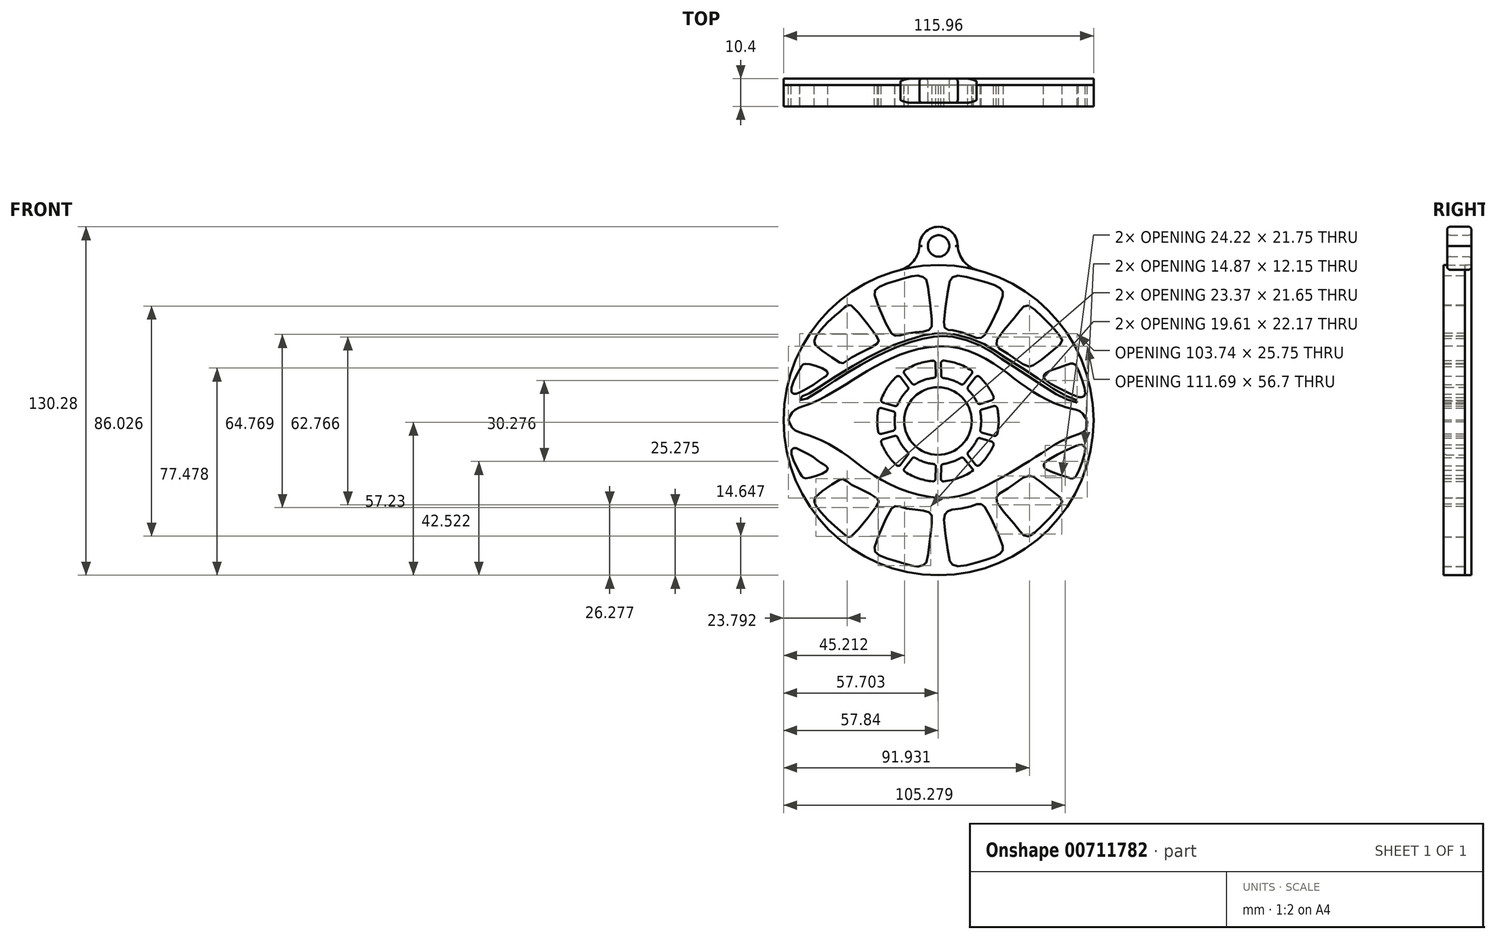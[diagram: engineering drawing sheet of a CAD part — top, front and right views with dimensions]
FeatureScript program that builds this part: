
annotation { "Feature Type Name" : "Feature", "Feature Type Description" : "" }
export const myFeature = defineFeature(function(context is Context, id is Id, definition is map)
    precondition{}
    {
        {
            var Q0;
            Q0=qCreatedBy(makeId("Front.planeOp"),FACE);
            var sketch = newSketch(context, id + "F0", { "sketchPlane" : qUnion([Q0])});
            skPoint(sketch, "E0.first.point", {"position": v(-56.19, 0) * mm});
            skPoint(sketch, "E0.second.point", {"position": v(55.8, -3.23) * mm});
            skPoint(sketch, "E0.third.point", {"position": v(-2.74, 55.09) * mm});
            skCircle(sketch, "E1", {"center": v(-0.25, -2.32) * mm, "radius": 12.63 * mm});
            skPoint(sketch, "E1.first.point", {"position": v(-12.67, 0) * mm});
            skPoint(sketch, "E1.second.point", {"position": v(12.27, -3.96) * mm});
            skPoint(sketch, "E1.third.point", {"position": v(2.35, 10.04) * mm});
            skFitSpline(sketch, "E2", {"points": [v(0, 25.6) * mm, v(22.08, 18.16) * mm, v(35.62, 8.4) * mm, v(48.16, 2.67) * mm, v(53.12, 1.17) * mm, v(55.8, -3.23) * mm], "startDerivative": vector(97.64, 3.3) * mm, "endDerivative": vector(12.94, -38.95) * mm});
            skFitSpline(sketch, "E3.MirrorCS", {"points": [v(0, 25.6) * mm, v(-22.75, 18.54) * mm, v(-38.1, 9.34) * mm, v(-48.7, 3.85) * mm, v(-54.13, 1.57) * mm, v(-56.3, -2.43) * mm], "startDerivative": vector(-92.15, -2.88) * mm, "endDerivative": vector(-12.94, -38.95) * mm});
            skFitSpline(sketch, "E4.MirrorCS", {"points": [v(0, -31.1) * mm, v(23.23, -23.62) * mm, v(36.64, -15.57) * mm, v(48.14, -8.8) * mm, v(55.17, -5.48) * mm, v(55.8, -1.41) * mm], "startDerivative": vector(97.64, -3.3) * mm, "endDerivative": vector(12.94, 38.95) * mm});
            skFitSpline(sketch, "E5.MirrorCS", {"points": [v(0, -31.1) * mm, v(-23.18, -23.24) * mm, v(-36.31, -13.78) * mm, v(-48.45, -7.65) * mm, v(-54.13, -5.41) * mm, v(-56.3, -1.41) * mm], "startDerivative": vector(-89.64, 6.19) * mm, "endDerivative": vector(-12.94, 38.95) * mm});
            skFitSpline(sketch, "E6", {"points": [v(-52, 5.4) * mm, v(-45.96, 7.88) * mm, v(-34.5, 15.43) * mm, v(-23.54, 21.65) * mm, v(-15.7, 25.25) * mm, v(-4.7, 28.68) * mm, v(0.44, 29.22) * mm], "startDerivative": vector(38.04, 9.99) * mm, "endDerivative": vector(34.79, 0.33) * mm});
            skFitSpline(sketch, "E7.MirrorCS", {"points": [v(51.82, 4.54) * mm, v(45.93, 6.75) * mm, v(33.9, 14.77) * mm, v(22.85, 21.49) * mm, v(15.76, 25.71) * mm, v(4.84, 29.15) * mm, v(-0.2, 29.2) * mm], "startDerivative": vector(-38.04, 9.99) * mm, "endDerivative": vector(-34.83, 0.37) * mm});
            skFitSpline(sketch, "E8", {"points": [v(-52.01, 8.4) * mm, v(-46.87, 11.2) * mm, v(-43.44, 13.7) * mm, v(-41.72, 14.8) * mm, v(-41.72, 16.2) * mm, v(-48.74, 19) * mm, v(-50.6, 18.84) * mm, v(-51.7, 17.29) * mm, v(-55.1, 9.31) * mm, v(-54.04, 7.78) * mm, v(-52.01, 8.4) * mm]});
            skFitSpline(sketch, "E9", {"points": [v(-45.87, 29.35) * mm, v(-40.77, 35.19) * mm, v(-36.51, 38.99) * mm, v(-34.47, 40.65) * mm, v(-33.45, 41.12) * mm, v(-32.25, 40.56) * mm, v(-22.8, 28.88) * mm, v(-22.42, 27.59) * mm, v(-23.26, 26.38) * mm, v(-31.7, 21.93) * mm, v(-34.29, 20.17) * mm, v(-35.96, 19.25) * mm, v(-37.62, 19.99) * mm, v(-45.96, 25.92) * mm, v(-46.52, 27.4) * mm, v(-45.87, 29.35) * mm]});
            skFitSpline(sketch, "E10", {"points": [v(-22.16, 47.89) * mm, v(-16.65, 49.92) * mm, v(-11.8, 51.3) * mm, v(-8.4, 52.08) * mm, v(-6.5, 51.82) * mm, v(-4.85, 50.9) * mm, v(-4.26, 49.4) * mm, v(-2.5, 34.19) * mm, v(-2.82, 32.55) * mm, v(-3.94, 31.57) * mm, v(-7.28, 30.98) * mm, v(-12.46, 30.26) * mm, v(-15.08, 29.54) * mm, v(-16.52, 29.6) * mm, v(-17.83, 30.72) * mm, v(-23.93, 44.67) * mm, v(-23.8, 46.44) * mm, v(-22.16, 47.89) * mm]});
            skFitSpline(sketch, "E11", {"points": [v(7.16, 52.01) * mm, v(14.24, 50.57) * mm, v(20.86, 48.54) * mm, v(23.28, 47.1) * mm, v(24, 46.05) * mm, v(24.07, 44.54) * mm, v(17.38, 30) * mm, v(16.07, 28.88) * mm, v(14.76, 28.62) * mm, v(11.75, 29.73) * mm, v(5.3, 31.6) * mm, v(3.6, 31.77) * mm, v(2.44, 32.42) * mm, v(2.05, 34.19) * mm, v(4.01, 49.2) * mm, v(5, 51.3) * mm, v(7.16, 52.01) * mm]});
            skFitSpline(sketch, "E12", {"points": [v(21.84, 28.1) * mm, v(29.38, 37.4) * mm, v(31.34, 40.02) * mm, v(32.78, 40.87) * mm, v(34.42, 40.48) * mm, v(39.47, 35.96) * mm, v(42.94, 32.35) * mm, v(45.37, 29.4) * mm, v(46.22, 27.83) * mm, v(45.56, 26.32) * mm, v(43.27, 24.55) * mm, v(39.53, 21.47) * mm, v(34.88, 18.2) * mm, v(33.96, 18.06) * mm, v(31.34, 19.05) * mm, v(26.69, 22.4) * mm, v(21.97, 25.4) * mm, v(21.64, 26.32) * mm, v(21.84, 28.1) * mm]});
            skFitSpline(sketch, "E13", {"points": [v(39.86, 15.5) * mm, v(48.7, 18.92) * mm, v(49.82, 19.24) * mm, v(50.87, 18.85) * mm, v(51.6, 18.13) * mm, v(54.84, 8.73) * mm, v(54.41, 6.99) * mm, v(53.17, 6.53) * mm, v(51.4, 6.99) * mm, v(44.78, 10.07) * mm, v(39.47, 13.54) * mm, v(39.27, 14.33) * mm, v(39.86, 15.5) * mm]});
            skFitSpline(sketch, "E14.MirrorC", {"points": [v(39.86, -20.15) * mm, v(48.7, -23.56) * mm, v(49.82, -23.88) * mm, v(50.87, -23.5) * mm, v(51.6, -22.77) * mm, v(54.84, -13.37) * mm, v(54.41, -11.63) * mm, v(53.17, -11.17) * mm, v(51.4, -11.63) * mm, v(44.78, -14.7) * mm, v(39.47, -18.18) * mm, v(39.27, -18.97) * mm, v(39.86, -20.15) * mm]});
            skFitSpline(sketch, "E15.MirrorC", {"points": [v(21.84, -32.73) * mm, v(29.38, -42.04) * mm, v(31.34, -44.66) * mm, v(32.78, -45.51) * mm, v(34.42, -45.12) * mm, v(39.47, -40.6) * mm, v(42.94, -37) * mm, v(45.37, -34.04) * mm, v(46.22, -32.47) * mm, v(45.56, -30.96) * mm, v(43.27, -29.2) * mm, v(39.53, -26.11) * mm, v(34.88, -22.84) * mm, v(33.96, -22.7) * mm, v(31.34, -23.69) * mm, v(26.69, -27.03) * mm, v(21.97, -30.04) * mm, v(21.64, -30.96) * mm, v(21.84, -32.73) * mm]});
            skFitSpline(sketch, "E16.MirrorC", {"points": [v(7.16, -56.65) * mm, v(14.24, -55.21) * mm, v(20.86, -53.18) * mm, v(23.28, -51.74) * mm, v(24, -50.69) * mm, v(24.07, -49.18) * mm, v(17.38, -34.63) * mm, v(16.07, -33.52) * mm, v(14.76, -33.26) * mm, v(11.75, -34.37) * mm, v(5.06, -35.48) * mm, v(3.5, -36) * mm, v(2.44, -37.06) * mm, v(2.05, -38.83) * mm, v(4.01, -53.83) * mm, v(5, -55.93) * mm, v(7.16, -56.65) * mm]});
            skFitSpline(sketch, "E17.MirrorC", {"points": [v(-22.16, -52.53) * mm, v(-16.65, -54.56) * mm, v(-11.8, -55.93) * mm, v(-8.4, -56.72) * mm, v(-6.5, -56.46) * mm, v(-4.85, -55.54) * mm, v(-4.26, -54.03) * mm, v(-2.5, -38.83) * mm, v(-2.82, -37.19) * mm, v(-3.94, -36.2) * mm, v(-7.28, -35.62) * mm, v(-12.46, -34.9) * mm, v(-15.08, -34.18) * mm, v(-16.52, -34.24) * mm, v(-17.83, -35.35) * mm, v(-23.93, -49.31) * mm, v(-23.8, -51.08) * mm, v(-22.16, -52.53) * mm]});
            skFitSpline(sketch, "E18.MirrorC", {"points": [v(-45.87, -33.99) * mm, v(-40.77, -39.83) * mm, v(-36.51, -43.63) * mm, v(-34.47, -45.3) * mm, v(-33.45, -45.76) * mm, v(-32.25, -45.2) * mm, v(-22.8, -33.52) * mm, v(-22.42, -32.23) * mm, v(-23.26, -31.02) * mm, v(-31.7, -26.57) * mm, v(-34.29, -24.81) * mm, v(-35.96, -23.89) * mm, v(-37.62, -24.63) * mm, v(-45.96, -30.56) * mm, v(-46.52, -32.04) * mm, v(-45.87, -33.99) * mm]});
            skFitSpline(sketch, "E19.MirrorC", {"points": [v(-52.01, -13.04) * mm, v(-46.87, -15.85) * mm, v(-43.44, -18.34) * mm, v(-41.72, -19.43) * mm, v(-41.72, -20.83) * mm, v(-48.74, -23.64) * mm, v(-50.6, -23.48) * mm, v(-51.7, -21.93) * mm, v(-55.1, -13.95) * mm, v(-54.04, -12.42) * mm, v(-52.01, -13.04) * mm]});
            skCircle(sketch, "E20", {"center": v(-0.25, -2.32) * mm, "radius": 58.34 * mm});
            skLineSegment(sketch, "E21.0", {"start": v(-9.43, 11) * mm, "end": v(-13.4, 16.13) * mm});
            skLineSegment(sketch, "E22.0", {"start": v(-10.98, 9.8) * mm, "end": v(-14.95, 14.97) * mm});
            skLineSegment(sketch, "E23.0", {"start": v(0.96, 13.83) * mm, "end": v(0.85, 20.35) * mm});
            skLineSegment(sketch, "E24.0", {"start": v(-0.95, 13.84) * mm, "end": v(-1.17, 20.31) * mm});
            skLineSegment(sketch, "E25.0", {"start": v(-15.55, 3.05) * mm, "end": v(-21.8, 4.82) * mm});
            skLineSegment(sketch, "E26.0", {"start": v(-16.08, 1.06) * mm, "end": v(-22.35, 2.79) * mm});
            skLineSegment(sketch, "E27.0", {"start": v(10.52, 9.8) * mm, "end": v(14.52, 14.93) * mm});
            skLineSegment(sketch, "E28.0", {"start": v(8.94, 11.01) * mm, "end": v(13.03, 16.08) * mm});
            skLineSegment(sketch, "E29.0", {"start": v(15.4, 1.82) * mm, "end": v(21.68, 3.5) * mm});
            skLineSegment(sketch, "E30.0", {"start": v(14.75, 3.82) * mm, "end": v(20.93, 5.8) * mm});
            skPoint(sketch, "E31.MirrorP", {"position": v(2.35, -14.68) * mm});
            skLineSegment(sketch, "E32.MirrorCS", {"start": v(10.52, -14.43) * mm, "end": v(14.52, -19.57) * mm});
            skLineSegment(sketch, "E33.MirrorCS", {"start": v(8.94, -15.65) * mm, "end": v(13.03, -20.72) * mm});
            skLineSegment(sketch, "E34.MirrorCS", {"start": v(-10.98, -14.44) * mm, "end": v(-14.95, -19.61) * mm});
            skLineSegment(sketch, "E35.MirrorCS", {"start": v(-9.43, -15.64) * mm, "end": v(-13.4, -20.77) * mm});
            skLineSegment(sketch, "E36.MirrorCS", {"start": v(-15.55, -7.7) * mm, "end": v(-21.8, -9.46) * mm});
            skLineSegment(sketch, "E37.MirrorCS", {"start": v(0.96, -18.47) * mm, "end": v(0.85, -24.99) * mm});
            skLineSegment(sketch, "E38.MirrorCS", {"start": v(-0.95, -18.48) * mm, "end": v(-1.17, -24.95) * mm});
            skLineSegment(sketch, "E39.MirrorCS", {"start": v(-16.08, -5.7) * mm, "end": v(-22.35, -7.43) * mm});
            skLineSegment(sketch, "E40.MirrorCS", {"start": v(15.4, -6.46) * mm, "end": v(21.68, -8.14) * mm});
            skLineSegment(sketch, "E41.MirrorCS", {"start": v(14.75, -8.46) * mm, "end": v(20.93, -10.43) * mm});
            skFitSpline(sketch, "E42.0", {"points": [v(-52.25, 6.37) * mm, v(-51.49, 6.57) * mm, v(-50.3, 6.95) * mm, v(-48.53, 7.68) * mm, v(-47.12, 8.37) * mm, v(-45.6, 9.23) * mm, v(-43.96, 10.25) * mm, v(-42.24, 11.4) * mm, v(-40.44, 12.62) * mm, v(-38.6, 13.9) * mm, v(-36.7, 15.18) * mm, v(-34.8, 16.44) * mm, v(-32.9, 17.62) * mm, v(-31.02, 18.74) * mm, v(-29.17, 19.78) * mm, v(-27.39, 20.76) * mm, v(-25.68, 21.67) * mm, v(-24.05, 22.52) * mm, v(-22.52, 23.3) * mm, v(-21.04, 24.02) * mm, v(-19.56, 24.72) * mm, v(-18.01, 25.4) * mm, v(-16.36, 26.07) * mm, v(-14.53, 26.77) * mm, v(-11.95, 27.7) * mm, v(-9.26, 28.56) * mm, v(-6.72, 29.25) * mm, v(-4.95, 29.67) * mm, v(-3.37, 29.95) * mm, v(-1.5, 30.17) * mm, v(-0.3, 30.2) * mm, v(0.44, 30.22) * mm]});
            skFitSpline(sketch, "E43.0", {"points": [v(52.07, 5.5) * mm, v(51.29, 5.71) * mm, v(50.09, 6.04) * mm, v(48.35, 6.7) * mm, v(47.19, 7.22) * mm, v(46.2, 7.74) * mm, v(45.16, 8.33) * mm, v(43.78, 9.19) * mm, v(42.02, 10.37) * mm, v(40.17, 11.65) * mm, v(38.28, 12.98) * mm, v(36.34, 14.34) * mm, v(34.39, 15.66) * mm, v(32.44, 16.9) * mm, v(30.53, 18.08) * mm, v(28.68, 19.18) * mm, v(26.9, 20.22) * mm, v(25.23, 21.2) * mm, v(23.68, 22.14) * mm, v(22.27, 23.04) * mm, v(20.92, 23.91) * mm, v(19.57, 24.77) * mm, v(18.15, 25.61) * mm, v(16.58, 26.44) * mm, v(14.81, 27.26) * mm, v(12.88, 28.03) * mm, v(10.88, 28.74) * mm, v(8.87, 29.34) * mm, v(7.24, 29.75) * mm, v(6, 30) * mm, v(5.12, 30.13) * mm, v(4.28, 30.22) * mm, v(3.23, 30.29) * mm, v(2.06, 30.28) * mm, v(0.84, 30.23) * mm, v(0.14, 30.2) * mm, v(-0.2, 30.2) * mm]});
            skLineSegment(sketch, "E44", {"start": v(-0.2, 29.2) * mm, "end": v(0.44, 29.22) * mm});
            skLineSegment(sketch, "E45", {"start": v(-52.25, 6.37) * mm, "end": v(-52, 5.4) * mm});
            skLineSegment(sketch, "E46", {"start": v(51.96, 5.53) * mm, "end": v(51.82, 4.54) * mm});
            skArc(sketch, "E47", {"start": v(-9.43, 11) * mm, "mid": v(-5.39, 13.01) * mm, "end": v(-0.95, 13.84) * mm});
            skArc(sketch, "E48", {"start": v(0.96, 13.83) * mm, "mid": v(5.14, 12.95) * mm, "end": v(8.94, 11.01) * mm});
            skArc(sketch, "E49", {"start": v(10.52, 9.8) * mm, "mid": v(12.98, 7.05) * mm, "end": v(14.75, 3.82) * mm});
            skArc(sketch, "E50", {"start": v(-15.55, 3.05) * mm, "mid": v(-13.71, 6.73) * mm, "end": v(-11, 9.82) * mm});
            skArc(sketch, "E51", {"start": v(-16.08, -5.7) * mm, "mid": v(-16.43, -2.32) * mm, "end": v(-16.08, 1.06) * mm});
            skArc(sketch, "E52", {"start": v(-15.55, -7.7) * mm, "mid": v(-13.71, -11.37) * mm, "end": v(-11, -14.46) * mm});
            skArc(sketch, "E53", {"start": v(-9.43, -15.64) * mm, "mid": v(-5.39, -17.65) * mm, "end": v(-0.95, -18.48) * mm});
            skArc(sketch, "E54", {"start": v(0.96, -18.47) * mm, "mid": v(5.14, -17.6) * mm, "end": v(8.94, -15.65) * mm});
            skArc(sketch, "E55", {"start": v(10.52, -14.43) * mm, "mid": v(12.98, -11.69) * mm, "end": v(14.75, -8.46) * mm});
            skArc(sketch, "E56", {"start": v(15.4, -6.46) * mm, "mid": v(15.93, -2.32) * mm, "end": v(15.4, 1.82) * mm});
            skArc(sketch, "E57", {"start": v(-13.4, 16.13) * mm, "mid": v(-7.59, 19.11) * mm, "end": v(-1.17, 20.31) * mm});
            skArc(sketch, "E58", {"start": v(0.85, 20.35) * mm, "mid": v(7.25, 19.1) * mm, "end": v(13.03, 16.08) * mm});
            skArc(sketch, "E59", {"start": v(-21.8, 4.82) * mm, "mid": v(-19.07, 10.37) * mm, "end": v(-14.95, 14.97) * mm});
            skArc(sketch, "E60", {"start": v(-22.35, -7.43) * mm, "mid": v(-22.93, -2.32) * mm, "end": v(-22.35, 2.79) * mm});
            skArc(sketch, "E61", {"start": v(-21.8, -9.46) * mm, "mid": v(-19.05, -15) * mm, "end": v(-14.92, -19.58) * mm});
            skArc(sketch, "E62", {"start": v(14.52, 14.93) * mm, "mid": v(18.3, 10.76) * mm, "end": v(20.92, 5.79) * mm});
            skArc(sketch, "E63", {"start": v(21.68, 3.5) * mm, "mid": v(22.44, -2.32) * mm, "end": v(21.68, -8.14) * mm});
            skArc(sketch, "E64", {"start": v(20.93, -10.43) * mm, "mid": v(18.27, -15.37) * mm, "end": v(14.47, -19.5) * mm});
            skArc(sketch, "E65", {"start": v(13.03, -20.72) * mm, "mid": v(7.25, -23.74) * mm, "end": v(0.85, -24.99) * mm});
            skArc(sketch, "E66", {"start": v(-1.17, -24.95) * mm, "mid": v(-7.59, -23.75) * mm, "end": v(-13.4, -20.77) * mm});
            skSolve(sketch);
        }
        {
            var Q0;
            Q0=qCreatedBy(makeId("Front.planeOp"),FACE);
            var sketch = newSketch(context, id + "F1", { "sketchPlane" : qUnion([Q0])});
            skCircle(sketch, "E67", {"center": v(0, -2) * mm, "radius": 57.98 * mm});
            skSolve(sketch);
        }
        {
            var Q0;
            Q0=qSketchRegion(id+"F1",true);
            extrude(context, id + "F2", {"entities" : qUnion([Q0]), "depth" : 8 * mm, "offsetDistance" : 25 * mm});
        }
        {
            var Q0;
            Q0=qSketchRegion(id+"F1",true);
            extrude(context, id + "F3", {"entities" : qUnion([Q0]), "oppositeDirection" : true, "depth" : 2.4 * mm, "offsetDistance" : 25 * mm});
        }
        {
            var Q0;
            Q0=makeQuery(id+"F0.imprint","IMPRINT",FACE,{"disambiguationData":[TD([[makeQuery(id+"F0.imprint","IMPRINT",EDGE,{"derivedFrom":sQuery(id+"F0.wireOp",EDGE,"E9")}),-1.0]])]});
            var Q1;
            Q1=makeQuery(id+"F0.imprint","IMPRINT",FACE,{"disambiguationData":[TD([[makeQuery(id+"F0.imprint","IMPRINT",EDGE,{"derivedFrom":sQuery(id+"F0.wireOp",EDGE,"E10")}),-1.0]])]});
            var Q2;
            Q2=makeQuery(id+"F0.imprint","IMPRINT",FACE,{"disambiguationData":[TD([[makeQuery(id+"F0.imprint","IMPRINT",EDGE,{"derivedFrom":sQuery(id+"F0.wireOp",EDGE,"E11")}),-1.0]])]});
            var Q3;
            Q3=makeQuery(id+"F0.imprint","IMPRINT",FACE,{"disambiguationData":[TD([[makeQuery(id+"F0.imprint","IMPRINT",EDGE,{"derivedFrom":sQuery(id+"F0.wireOp",EDGE,"E12")}),-1.0]])]});
            var Q4;
            {var subQ7=sQuery(id+"F0.wireOp",EDGE,"E3.MirrorCS");var subQ8=sQuery(id+"F0.wireOp",EDGE,"E2");var subQ9=makeQuery(id+"F0.imprint","INTERSECT",VERTEX,{"derivedFrom":[subQ8,subQ7]});Q4=makeQuery(id+"F0.imprint","IMPRINT",FACE,{"disambiguationData":[TD([[makeQuery(id+"F0.imprint","IMPRINT",EDGE,{"disambiguationData":[TD([[subQ9,-1.0]])],"derivedFrom":subQ8}),-1.0]])]});}
            var Q5;
            {var subQ4=sQuery(id+"F0.wireOp",EDGE,"E22.0");Q5=makeQuery(id+"F0.imprint","IMPRINT",FACE,{"disambiguationData":[TD([[makeQuery(id+"F0.imprint","IMPRINT",EDGE,{"derivedFrom":subQ4}),-1.0]])]});}
            var Q6;
            {var subQ0=sQuery(id+"F0.wireOp",EDGE,"E23.0");Q6=makeQuery(id+"F0.imprint","IMPRINT",FACE,{"disambiguationData":[TD([[makeQuery(id+"F0.imprint","IMPRINT",EDGE,{"derivedFrom":subQ0}),1.0]])]});}
            var Q7;
            {var subQ1=sQuery(id+"F0.wireOp",EDGE,"E27.0");Q7=makeQuery(id+"F0.imprint","IMPRINT",FACE,{"disambiguationData":[TD([[makeQuery(id+"F0.imprint","IMPRINT",EDGE,{"derivedFrom":subQ1}),1.0]])]});}
            var Q8;
            {var subQ2=sQuery(id+"F0.wireOp",EDGE,"E29.0");Q8=makeQuery(id+"F0.imprint","IMPRINT",FACE,{"disambiguationData":[TD([[makeQuery(id+"F0.imprint","IMPRINT",EDGE,{"derivedFrom":subQ2}),1.0]])]});}
            var Q9;
            {var subQ4=sQuery(id+"F0.wireOp",EDGE,"E40.MirrorCS");Q9=makeQuery(id+"F0.imprint","IMPRINT",FACE,{"disambiguationData":[TD([[makeQuery(id+"F0.imprint","IMPRINT",EDGE,{"derivedFrom":subQ4}),-1.0]])]});}
            var Q10;
            Q10=makeQuery(id+"F0.imprint","IMPRINT",FACE,{"disambiguationData":[TD([[makeQuery(id+"F0.imprint","IMPRINT",EDGE,{"derivedFrom":sQuery(id+"F0.wireOp",EDGE,"fab38fe7-764f-41c1-85e6-31b15052e3932.MirrorCS")}),1.0]])]});
            var Q11;
            Q11=makeQuery(id+"F0.imprint","IMPRINT",FACE,{"disambiguationData":[TD([[makeQuery(id+"F0.imprint","IMPRINT",EDGE,{"derivedFrom":sQuery(id+"F0.wireOp",EDGE,"fab38fe7-764f-41c1-85e6-31b15052e3934.MirrorCS")}),1.0]])]});
            var Q12;
            {var subQ0=sQuery(id+"F0.wireOp",EDGE,"fab38fe7-764f-41c1-85e6-31b15052e3930.MirrorCS");Q12=makeQuery(id+"F0.imprint","IMPRINT",FACE,{"disambiguationData":[TD([[makeQuery(id+"F0.imprint","IMPRINT",EDGE,{"derivedFrom":subQ0}),1.0]])]});}
            var Q13;
            Q13=makeQuery(id+"F0.imprint","IMPRINT",FACE,{"disambiguationData":[TD([[makeQuery(id+"F0.imprint","IMPRINT",EDGE,{"derivedFrom":sQuery(id+"F0.wireOp",EDGE,"fab38fe7-764f-41c1-85e6-31b15052e3936.MirrorCS")}),1.0]])]});
            var Q14;
            {var subQ1=sQuery(id+"F0.wireOp",EDGE,"E25.0");Q14=makeQuery(id+"F0.imprint","IMPRINT",FACE,{"disambiguationData":[TD([[makeQuery(id+"F0.imprint","IMPRINT",EDGE,{"derivedFrom":subQ1}),1.0]])]});}
            var Q15;
            Q15=makeQuery(id+"F0.imprint","IMPRINT",FACE,{"disambiguationData":[TD([[makeQuery(id+"F0.imprint","IMPRINT",EDGE,{"derivedFrom":sQuery(id+"F0.wireOp",EDGE,"E1")}),-1.0]])]});
            var Q16;
            Q16=makeQuery(id+"F0.imprint","IMPRINT",FACE,{"disambiguationData":[TD([[makeQuery(id+"F0.imprint","IMPRINT",EDGE,{"derivedFrom":sQuery(id+"F0.wireOp",EDGE,"E8")}),1.0]])]});
            var Q17;
            Q17=makeQuery(id+"F0.imprint","IMPRINT",FACE,{"disambiguationData":[TD([[makeQuery(id+"F0.imprint","IMPRINT",EDGE,{"derivedFrom":sQuery(id+"F0.wireOp",EDGE,"E13")}),-1.0]])]});
            var Q18;
            Q18=makeQuery(id+"F0.imprint","IMPRINT",FACE,{"disambiguationData":[TD([[makeQuery(id+"F0.imprint","IMPRINT",EDGE,{"derivedFrom":sQuery(id+"F0.wireOp",EDGE,"E14.MirrorC")}),1.0]])]});
            var Q19;
            Q19=makeQuery(id+"F0.imprint","IMPRINT",FACE,{"disambiguationData":[TD([[makeQuery(id+"F0.imprint","IMPRINT",EDGE,{"derivedFrom":sQuery(id+"F0.wireOp",EDGE,"E15.MirrorC")}),1.0]])]});
            var Q20;
            Q20=makeQuery(id+"F0.imprint","IMPRINT",FACE,{"disambiguationData":[TD([[makeQuery(id+"F0.imprint","IMPRINT",EDGE,{"derivedFrom":sQuery(id+"F0.wireOp",EDGE,"E16.MirrorC")}),1.0]])]});
            var Q21;
            Q21=makeQuery(id+"F0.imprint","IMPRINT",FACE,{"disambiguationData":[TD([[makeQuery(id+"F0.imprint","IMPRINT",EDGE,{"derivedFrom":sQuery(id+"F0.wireOp",EDGE,"E17.MirrorC")}),1.0]])]});
            var Q22;
            Q22=makeQuery(id+"F0.imprint","IMPRINT",FACE,{"disambiguationData":[TD([[makeQuery(id+"F0.imprint","IMPRINT",EDGE,{"derivedFrom":sQuery(id+"F0.wireOp",EDGE,"E18.MirrorC")}),1.0]])]});
            var Q23;
            Q23=makeQuery(id+"F0.imprint","IMPRINT",FACE,{"disambiguationData":[TD([[makeQuery(id+"F0.imprint","IMPRINT",EDGE,{"derivedFrom":sQuery(id+"F0.wireOp",EDGE,"E19.MirrorC")}),-1.0]])]});
            extrude(context, id + "F4", {"entities" : qUnion([Q0, Q1, Q2, Q3, Q4, Q5, Q6, Q7, Q8, Q9, Q10, Q11, Q12, Q13, Q14, Q15, Q16, Q17, Q18, Q19, Q20, Q21, Q22, Q23]), "operationType" : NewBodyOperationType.REMOVE, "depth" : 54 * mm, "offsetDistance" : 25 * mm});
        }
        {
            var Q0;
            Q0=qCreatedBy(makeId("Front.planeOp"),FACE);
            var sketch = newSketch(context, id + "F5", { "sketchPlane" : qUnion([Q0])});
            skFitSpline(sketch, "E68", {"points": [v(51.73, 4.62) * mm, v(45.97, 6.68) * mm, v(33.43, 14.5) * mm, v(22.66, 21.52) * mm, v(15.59, 25.92) * mm, v(4.74, 29.24) * mm, v(0, 29.34) * mm, v(-5.9, 28.46) * mm, v(-15.38, 25.43) * mm, v(-23.69, 21.62) * mm, v(-34.34, 15.57) * mm, v(-45.96, 8.04) * mm, v(-52.01, 5.48) * mm], "startDerivative": vector(-81.76, 20.23) * mm, "endDerivative": vector(1.8, 51.56) * mm});
            skFitSpline(sketch, "E69", {"points": [v(-52.01, 5.48) * mm, v(-52.01, 6.3) * mm, v(-49.46, 7.46) * mm, v(-47.8, 8.36) * mm, v(-34.8, 16.66) * mm, v(-23.3, 23.06) * mm, v(-14.34, 27) * mm, v(-4.24, 29.96) * mm, v(0, 30.37) * mm, v(4.88, 30.21) * mm, v(15.97, 26.92) * mm, v(22.66, 22.8) * mm, v(34.12, 15.67) * mm, v(46.45, 7.7) * mm, v(51.54, 5.48) * mm, v(52.15, 4.94) * mm, v(51.73, 4.62) * mm], "startDerivative": vector(-11.3, 39.4) * mm, "endDerivative": vector(-33.35, -16.31) * mm});
            skSolve(sketch);
        }
        {
            var Q0;
            Q0=qSketchRegion(id+"F5",true);
            extrude(context, id + "F6", {"entities" : qUnion([Q0]), "operationType" : NewBodyOperationType.REMOVE, "depth" : 55 * mm, "offsetDistance" : 25 * mm});
        }
        {
            var Q0;
            Q0=makeQuery(id+"F3.opExtrude","CAP_FACE",FACE,{"disambiguationData":[OSD([sQuery(id+"F1.wireOp",EDGE,"E67")])],"isStart":false});
            var sketch = newSketch(context, id + "F7", { "sketchPlane" : qUnion([Q0])});
            skCircle(sketch, "E70", {"center": v(0, 63.14) * mm, "radius": 4 * mm});
            skCircle(sketch, "E71", {"center": v(0, 63.14) * mm, "radius": 7.16 * mm});
            skLineSegment(sketch, "E72", {"start": v(0, 63.14) * mm, "end": v(0, 50.53) * mm, "construction": true});
            skArc(sketch, "E73", {"start": v(7.16, 63.14) * mm, "mid": v(9.57, 57.24) * mm, "end": v(15.05, 53.99) * mm});
            skArc(sketch, "E74.MirrorCS", {"start": v(-7.16, 63.14) * mm, "mid": v(-9.57, 57.24) * mm, "end": v(-15.05, 53.99) * mm});
            skArc(sketch, "E75", {"start": v(15.05, 53.99) * mm, "mid": v(0, 55.7) * mm, "end": v(-15.05, 53.99) * mm});
            skSolve(sketch);
        }
        {
            var Q0;
            Q0=makeQuery(id+"F7.imprint","IMPRINT",FACE,{"disambiguationData":[TD([[makeQuery(id+"F7.imprint","IMPRINT",EDGE,{"derivedFrom":sQuery(id+"F7.wireOp",EDGE,"E70")}),-1.0]])]});
            var Q1;
            {var subQ0=sQuery(id+"F7.wireOp",EDGE,"4d7e6d00-9c74-48b9-857c-3da9c287da2b0.MirrorCS");var subQ1=sQuery(id+"F7.wireOp",EDGE,"E71");var subQ2=makeQuery(id+"F7.imprint","INTERSECT",VERTEX,{"disambiguationData":[OD(1.0)],"derivedFrom":[subQ1,subQ0]});Q1=makeQuery(id+"F7.imprint","IMPRINT",FACE,{"disambiguationData":[TD([[makeQuery(id+"F7.imprint","IMPRINT",EDGE,{"disambiguationData":[TD([[subQ2,-1.0]])],"derivedFrom":subQ1}),-1.0]])]});}
            var Q2;
            {var subQ0=sQuery(id+"F7.wireOp",EDGE,"TQhcUTrG-cz5W-IBKC-6cSZ-7010gBsPSDav");var subQ1=sQuery(id+"F7.wireOp",EDGE,"E71");var subQ2=makeQuery(id+"F7.imprint","INTERSECT",VERTEX,{"disambiguationData":[OD(1.0)],"derivedFrom":[subQ1,subQ0]});Q2=makeQuery(id+"F7.imprint","IMPRINT",FACE,{"disambiguationData":[TD([[makeQuery(id+"F7.imprint","IMPRINT",EDGE,{"disambiguationData":[TD([[subQ2,1.0]])],"derivedFrom":subQ1}),-1.0]])]});}
            var Q3;
            {var subQ0=sQuery(id+"F7.wireOp",EDGE,"5f5PjPiJ-K3tQ-l48y-JfNq-w7BlEygly8IJ");var subQ1=sQuery(id+"F7.wireOp",EDGE,"E71");var subQ2=makeQuery(id+"F7.imprint","INTERSECT",VERTEX,{"derivedFrom":[subQ1,subQ0]});Q3=makeQuery(id+"F7.imprint","IMPRINT",FACE,{"disambiguationData":[TD([[makeQuery(id+"F7.imprint","IMPRINT",EDGE,{"disambiguationData":[TD([[subQ2,1.0]])],"derivedFrom":subQ1}),-1.0]])]});}
            var Q4;
            {var subQ0=sQuery(id+"F7.wireOp",EDGE,"x1zDsQyn-PUHO-lvpH-2OqF-o5lNL2ItqWKP");var subQ1=sQuery(id+"F7.wireOp",EDGE,"E71");var subQ2=makeQuery(id+"F7.imprint","INTERSECT",VERTEX,{"derivedFrom":[subQ1,subQ0]});Q4=makeQuery(id+"F7.imprint","IMPRINT",FACE,{"disambiguationData":[TD([[makeQuery(id+"F7.imprint","IMPRINT",EDGE,{"disambiguationData":[TD([[subQ2,-1.0]])],"derivedFrom":subQ1}),-1.0]])]});}
            extrude(context, id + "F8", {"entities" : qUnion([Q0, Q1, Q2, Q3, Q4]), "oppositeDirection" : true, "depth" : 9 * mm, "offsetDistance" : 25 * mm});
        }
        {
            var Q0;
            Q0=makeQuery(id+"F8.opExtrude","CAP_EDGE",EDGE,{"disambiguationData":[OSD([sQuery(id+"F7.wireOp",EDGE,"5f5PjPiJ-K3tQ-l48y-JfNq-w7BlEygly8IJ")])],"isStart":false});
            var Q1;
            Q1=makeQuery(id+"F8.opExtrude","CAP_EDGE",EDGE,{"disambiguationData":[OSD([sQuery(id+"F7.wireOp",EDGE,"E71")])],"isStart":false});
            var Q2;
            Q2=makeQuery(id+"F8.opExtrude","CAP_EDGE",EDGE,{"disambiguationData":[OSD([sQuery(id+"F7.wireOp",EDGE,"x1zDsQyn-PUHO-lvpH-2OqF-o5lNL2ItqWKP")])],"isStart":false});
            var Q3;
            Q3=makeQuery(id+"F8.opExtrude","CAP_EDGE",EDGE,{"disambiguationData":[OSD([sQuery(id+"F7.wireOp",EDGE,"E70")])],"isStart":false});
            var Q4;
            Q4=makeQuery(id+"F8.opExtrude","CAP_EDGE",EDGE,{"disambiguationData":[OSD([sQuery(id+"F7.wireOp",EDGE,"E70")])],"isStart":true});
            var Q5;
            Q5=makeQuery(id+"F8.opExtrude","CAP_EDGE",EDGE,{"disambiguationData":[OSD([sQuery(id+"F7.wireOp",EDGE,"E71")])],"isStart":true});
            var Q6;
            Q6=makeQuery(id+"F8.opExtrude","CAP_EDGE",EDGE,{"disambiguationData":[OSD([sQuery(id+"F7.wireOp",EDGE,"x1zDsQyn-PUHO-lvpH-2OqF-o5lNL2ItqWKP")])],"isStart":true});
            var Q7;
            Q7=makeQuery(id+"F8.opExtrude","CAP_EDGE",EDGE,{"disambiguationData":[OSD([sQuery(id+"F7.wireOp",EDGE,"5f5PjPiJ-K3tQ-l48y-JfNq-w7BlEygly8IJ")])],"isStart":true});
            fillet(context, id + "F9", {"entities" : qUnion([Q0, Q1, Q2, Q3, Q4, Q5, Q6, Q7]), "radius" : 1 * mm, "tangentPropagation" : true, "allowEdgeOverflow" : false});
        }
        {
            var Q0;
            Q0=makeQuery(id+"F4.boolean.opBoolean","COPY",EDGE,{"derivedFrom":makeQuery(id+"F4.opExtrude","SWEPT_EDGE",EDGE,{"disambiguationData":[OSD([sQuery(id+"F0.wireOp",EDGE,"E24.0"),sQuery(id+"F0.wireOp",EDGE,"E57")])]})});
            var Q1;
            Q1=makeQuery(id+"F4.boolean.opBoolean","COPY",EDGE,{"derivedFrom":makeQuery(id+"F4.opExtrude","SWEPT_EDGE",EDGE,{"disambiguationData":[OSD([sQuery(id+"F0.wireOp",EDGE,"E24.0"),sQuery(id+"F0.wireOp",EDGE,"E47")])]})});
            var Q2;
            Q2=makeQuery(id+"F4.boolean.opBoolean","COPY",EDGE,{"derivedFrom":makeQuery(id+"F4.opExtrude","SWEPT_EDGE",EDGE,{"disambiguationData":[OSD([sQuery(id+"F0.wireOp",EDGE,"E21.0"),sQuery(id+"F0.wireOp",EDGE,"E47")])]})});
            var Q3;
            Q3=makeQuery(id+"F4.boolean.opBoolean","COPY",EDGE,{"derivedFrom":makeQuery(id+"F4.opExtrude","SWEPT_EDGE",EDGE,{"disambiguationData":[OSD([sQuery(id+"F0.wireOp",EDGE,"E21.0"),sQuery(id+"F0.wireOp",EDGE,"E57")])]})});
            var Q4;
            Q4=makeQuery(id+"F4.boolean.opBoolean","COPY",EDGE,{"derivedFrom":makeQuery(id+"F4.opExtrude","SWEPT_EDGE",EDGE,{"disambiguationData":[OSD([sQuery(id+"F0.wireOp",EDGE,"E22.0"),sQuery(id+"F0.wireOp",EDGE,"E50")])]})});
            var Q5;
            Q5=makeQuery(id+"F4.boolean.opBoolean","COPY",EDGE,{"derivedFrom":makeQuery(id+"F4.opExtrude","SWEPT_EDGE",EDGE,{"disambiguationData":[OSD([sQuery(id+"F0.wireOp",EDGE,"E22.0"),sQuery(id+"F0.wireOp",EDGE,"E59")])]})});
            var Q6;
            Q6=makeQuery(id+"F4.boolean.opBoolean","COPY",EDGE,{"derivedFrom":makeQuery(id+"F4.opExtrude","SWEPT_EDGE",EDGE,{"disambiguationData":[OSD([sQuery(id+"F0.wireOp",EDGE,"E26.0"),sQuery(id+"F0.wireOp",EDGE,"E51")])]})});
            var Q7;
            Q7=makeQuery(id+"F4.boolean.opBoolean","COPY",EDGE,{"derivedFrom":makeQuery(id+"F4.opExtrude","SWEPT_EDGE",EDGE,{"disambiguationData":[OSD([sQuery(id+"F0.wireOp",EDGE,"E26.0"),sQuery(id+"F0.wireOp",EDGE,"E60")])]})});
            var Q8;
            Q8=makeQuery(id+"F4.boolean.opBoolean","COPY",EDGE,{"derivedFrom":makeQuery(id+"F4.opExtrude","SWEPT_EDGE",EDGE,{"disambiguationData":[OSD([sQuery(id+"F0.wireOp",EDGE,"E25.0"),sQuery(id+"F0.wireOp",EDGE,"E59")])]})});
            var Q9;
            Q9=makeQuery(id+"F4.boolean.opBoolean","COPY",EDGE,{"derivedFrom":makeQuery(id+"F4.opExtrude","SWEPT_EDGE",EDGE,{"disambiguationData":[OSD([sQuery(id+"F0.wireOp",EDGE,"E39.MirrorCS"),sQuery(id+"F0.wireOp",EDGE,"E60")])]})});
            var Q10;
            Q10=makeQuery(id+"F4.boolean.opBoolean","COPY",EDGE,{"derivedFrom":makeQuery(id+"F4.opExtrude","SWEPT_EDGE",EDGE,{"disambiguationData":[OSD([sQuery(id+"F0.wireOp",EDGE,"E39.MirrorCS"),sQuery(id+"F0.wireOp",EDGE,"E51")])]})});
            var Q11;
            Q11=makeQuery(id+"F4.boolean.opBoolean","COPY",EDGE,{"derivedFrom":makeQuery(id+"F4.opExtrude","SWEPT_EDGE",EDGE,{"disambiguationData":[OSD([sQuery(id+"F0.wireOp",EDGE,"E36.MirrorCS"),sQuery(id+"F0.wireOp",EDGE,"E61")])]})});
            var Q12;
            Q12=makeQuery(id+"F4.boolean.opBoolean","COPY",EDGE,{"derivedFrom":makeQuery(id+"F4.opExtrude","SWEPT_EDGE",EDGE,{"disambiguationData":[OSD([sQuery(id+"F0.wireOp",EDGE,"E34.MirrorCS"),sQuery(id+"F0.wireOp",EDGE,"E61")])]})});
            var Q13;
            Q13=makeQuery(id+"F4.boolean.opBoolean","COPY",EDGE,{"derivedFrom":makeQuery(id+"F4.opExtrude","SWEPT_EDGE",EDGE,{"disambiguationData":[OSD([sQuery(id+"F0.wireOp",EDGE,"E35.MirrorCS"),sQuery(id+"F0.wireOp",EDGE,"E66")])]})});
            var Q14;
            Q14=makeQuery(id+"F4.boolean.opBoolean","COPY",EDGE,{"derivedFrom":makeQuery(id+"F4.opExtrude","SWEPT_EDGE",EDGE,{"disambiguationData":[OSD([sQuery(id+"F0.wireOp",EDGE,"E38.MirrorCS"),sQuery(id+"F0.wireOp",EDGE,"E66")])]})});
            var Q15;
            Q15=makeQuery(id+"F4.boolean.opBoolean","COPY",EDGE,{"derivedFrom":makeQuery(id+"F4.opExtrude","SWEPT_EDGE",EDGE,{"disambiguationData":[OSD([sQuery(id+"F0.wireOp",EDGE,"E37.MirrorCS"),sQuery(id+"F0.wireOp",EDGE,"E65")])]})});
            var Q16;
            Q16=makeQuery(id+"F4.boolean.opBoolean","COPY",EDGE,{"derivedFrom":makeQuery(id+"F4.opExtrude","SWEPT_EDGE",EDGE,{"disambiguationData":[OSD([sQuery(id+"F0.wireOp",EDGE,"E32.MirrorCS"),sQuery(id+"F0.wireOp",EDGE,"E64")])]})});
            var Q17;
            Q17=makeQuery(id+"F4.boolean.opBoolean","COPY",EDGE,{"derivedFrom":makeQuery(id+"F4.opExtrude","SWEPT_EDGE",EDGE,{"disambiguationData":[OSD([sQuery(id+"F0.wireOp",EDGE,"E32.MirrorCS"),sQuery(id+"F0.wireOp",EDGE,"E55")])]})});
            var Q18;
            Q18=makeQuery(id+"F4.boolean.opBoolean","COPY",EDGE,{"derivedFrom":makeQuery(id+"F4.opExtrude","SWEPT_EDGE",EDGE,{"disambiguationData":[OSD([sQuery(id+"F0.wireOp",EDGE,"E40.MirrorCS"),sQuery(id+"F0.wireOp",EDGE,"E56")])]})});
            var Q19;
            Q19=makeQuery(id+"F4.boolean.opBoolean","COPY",EDGE,{"derivedFrom":makeQuery(id+"F4.opExtrude","SWEPT_EDGE",EDGE,{"disambiguationData":[OSD([sQuery(id+"F0.wireOp",EDGE,"E41.MirrorCS"),sQuery(id+"F0.wireOp",EDGE,"E55")])]})});
            var Q20;
            Q20=makeQuery(id+"F4.boolean.opBoolean","COPY",EDGE,{"derivedFrom":makeQuery(id+"F4.opExtrude","SWEPT_EDGE",EDGE,{"disambiguationData":[OSD([sQuery(id+"F0.wireOp",EDGE,"E40.MirrorCS"),sQuery(id+"F0.wireOp",EDGE,"E63")])]})});
            var Q21;
            Q21=makeQuery(id+"F4.boolean.opBoolean","COPY",EDGE,{"derivedFrom":makeQuery(id+"F4.opExtrude","SWEPT_EDGE",EDGE,{"disambiguationData":[OSD([sQuery(id+"F0.wireOp",EDGE,"E29.0"),sQuery(id+"F0.wireOp",EDGE,"E56")])]})});
            var Q22;
            Q22=makeQuery(id+"F4.boolean.opBoolean","COPY",EDGE,{"derivedFrom":makeQuery(id+"F4.opExtrude","SWEPT_EDGE",EDGE,{"disambiguationData":[OSD([sQuery(id+"F0.wireOp",EDGE,"E30.0"),sQuery(id+"F0.wireOp",EDGE,"E49")])]})});
            var Q23;
            Q23=makeQuery(id+"F4.boolean.opBoolean","COPY",EDGE,{"derivedFrom":makeQuery(id+"F4.opExtrude","SWEPT_EDGE",EDGE,{"disambiguationData":[OSD([sQuery(id+"F0.wireOp",EDGE,"E27.0"),sQuery(id+"F0.wireOp",EDGE,"E49")])]})});
            var Q24;
            Q24=makeQuery(id+"F4.boolean.opBoolean","COPY",EDGE,{"derivedFrom":makeQuery(id+"F4.opExtrude","SWEPT_EDGE",EDGE,{"disambiguationData":[OSD([sQuery(id+"F0.wireOp",EDGE,"E28.0"),sQuery(id+"F0.wireOp",EDGE,"E48")])]})});
            var Q25;
            Q25=makeQuery(id+"F4.boolean.opBoolean","COPY",EDGE,{"derivedFrom":makeQuery(id+"F4.opExtrude","SWEPT_EDGE",EDGE,{"disambiguationData":[OSD([sQuery(id+"F0.wireOp",EDGE,"E23.0"),sQuery(id+"F0.wireOp",EDGE,"E48")])]})});
            var Q26;
            Q26=makeQuery(id+"F4.boolean.opBoolean","COPY",EDGE,{"derivedFrom":makeQuery(id+"F4.opExtrude","SWEPT_EDGE",EDGE,{"disambiguationData":[OSD([sQuery(id+"F0.wireOp",EDGE,"E25.0"),sQuery(id+"F0.wireOp",EDGE,"E50")])]})});
            var Q27;
            Q27=makeQuery(id+"F4.boolean.opBoolean","COPY",EDGE,{"derivedFrom":makeQuery(id+"F4.opExtrude","SWEPT_EDGE",EDGE,{"disambiguationData":[OSD([sQuery(id+"F0.wireOp",EDGE,"E30.0"),sQuery(id+"F0.wireOp",EDGE,"E62")])]})});
            var Q28;
            Q28=makeQuery(id+"F4.boolean.opBoolean","COPY",EDGE,{"derivedFrom":makeQuery(id+"F4.opExtrude","SWEPT_EDGE",EDGE,{"disambiguationData":[OSD([sQuery(id+"F0.wireOp",EDGE,"E27.0"),sQuery(id+"F0.wireOp",EDGE,"E62")])]})});
            var Q29;
            Q29=makeQuery(id+"F4.boolean.opBoolean","COPY",EDGE,{"derivedFrom":makeQuery(id+"F4.opExtrude","SWEPT_EDGE",EDGE,{"disambiguationData":[OSD([sQuery(id+"F0.wireOp",EDGE,"E38.MirrorCS"),sQuery(id+"F0.wireOp",EDGE,"E53")])]})});
            var Q30;
            Q30=makeQuery(id+"F4.boolean.opBoolean","COPY",EDGE,{"derivedFrom":makeQuery(id+"F4.opExtrude","SWEPT_EDGE",EDGE,{"disambiguationData":[OSD([sQuery(id+"F0.wireOp",EDGE,"E35.MirrorCS"),sQuery(id+"F0.wireOp",EDGE,"E53")])]})});
            var Q31;
            Q31=makeQuery(id+"F4.boolean.opBoolean","COPY",EDGE,{"derivedFrom":makeQuery(id+"F4.opExtrude","SWEPT_EDGE",EDGE,{"disambiguationData":[OSD([sQuery(id+"F0.wireOp",EDGE,"E34.MirrorCS"),sQuery(id+"F0.wireOp",EDGE,"E52")])]})});
            var Q32;
            Q32=makeQuery(id+"F4.boolean.opBoolean","COPY",EDGE,{"derivedFrom":makeQuery(id+"F4.opExtrude","SWEPT_EDGE",EDGE,{"disambiguationData":[OSD([sQuery(id+"F0.wireOp",EDGE,"E36.MirrorCS"),sQuery(id+"F0.wireOp",EDGE,"E52")])]})});
            var Q33;
            Q33=makeQuery(id+"F4.boolean.opBoolean","COPY",EDGE,{"derivedFrom":makeQuery(id+"F4.opExtrude","SWEPT_EDGE",EDGE,{"disambiguationData":[OSD([sQuery(id+"F0.wireOp",EDGE,"E29.0"),sQuery(id+"F0.wireOp",EDGE,"E63")])]})});
            var Q34;
            Q34=makeQuery(id+"F4.boolean.opBoolean","COPY",EDGE,{"derivedFrom":makeQuery(id+"F4.opExtrude","SWEPT_EDGE",EDGE,{"disambiguationData":[OSD([sQuery(id+"F0.wireOp",EDGE,"E41.MirrorCS"),sQuery(id+"F0.wireOp",EDGE,"E64")])]})});
            var Q35;
            Q35=makeQuery(id+"F4.boolean.opBoolean","COPY",EDGE,{"derivedFrom":makeQuery(id+"F4.opExtrude","SWEPT_EDGE",EDGE,{"disambiguationData":[OSD([sQuery(id+"F0.wireOp",EDGE,"E23.0"),sQuery(id+"F0.wireOp",EDGE,"E58")])]})});
            var Q36;
            Q36=makeQuery(id+"F4.boolean.opBoolean","COPY",EDGE,{"derivedFrom":makeQuery(id+"F4.opExtrude","SWEPT_EDGE",EDGE,{"disambiguationData":[OSD([sQuery(id+"F0.wireOp",EDGE,"E28.0"),sQuery(id+"F0.wireOp",EDGE,"E58")])]})});
            var Q37;
            Q37=makeQuery(id+"F4.boolean.opBoolean","COPY",EDGE,{"derivedFrom":makeQuery(id+"F4.opExtrude","SWEPT_EDGE",EDGE,{"disambiguationData":[OSD([sQuery(id+"F0.wireOp",EDGE,"E37.MirrorCS"),sQuery(id+"F0.wireOp",EDGE,"E54")])]})});
            var Q38;
            Q38=makeQuery(id+"F4.boolean.opBoolean","COPY",EDGE,{"derivedFrom":makeQuery(id+"F4.opExtrude","SWEPT_EDGE",EDGE,{"disambiguationData":[OSD([sQuery(id+"F0.wireOp",EDGE,"E33.MirrorCS"),sQuery(id+"F0.wireOp",EDGE,"E54")])]})});
            var Q39;
            Q39=makeQuery(id+"F4.boolean.opBoolean","INTERSECT",EDGE,{"derivedFrom":[makeQuery(id+"F2.opExtrude","CAP_FACE",FACE,{"disambiguationData":[OSD([sQuery(id+"F1.wireOp",EDGE,"E67")])],"isStart":false}),makeQuery(id+"F4.opExtrude","SWEPT_FACE",FACE,{"disambiguationData":[OSD([sQuery(id+"F0.wireOp",EDGE,"E1")])]})]});
            fillet(context, id + "F10", {"entities" : qUnion([Q0, Q1, Q2, Q3, Q4, Q5, Q6, Q7, Q8, Q9, Q10, Q11, Q12, Q13, Q14, Q15, Q16, Q17, Q18, Q19, Q20, Q21, Q22, Q23, Q24, Q25, Q26, Q27, Q28, Q29, Q30, Q31, Q32, Q33, Q34, Q35, Q36, Q37, Q38, Q39]), "radius" : 1 * mm, "tangentPropagation" : true, "allowEdgeOverflow" : false});
        }
    });
